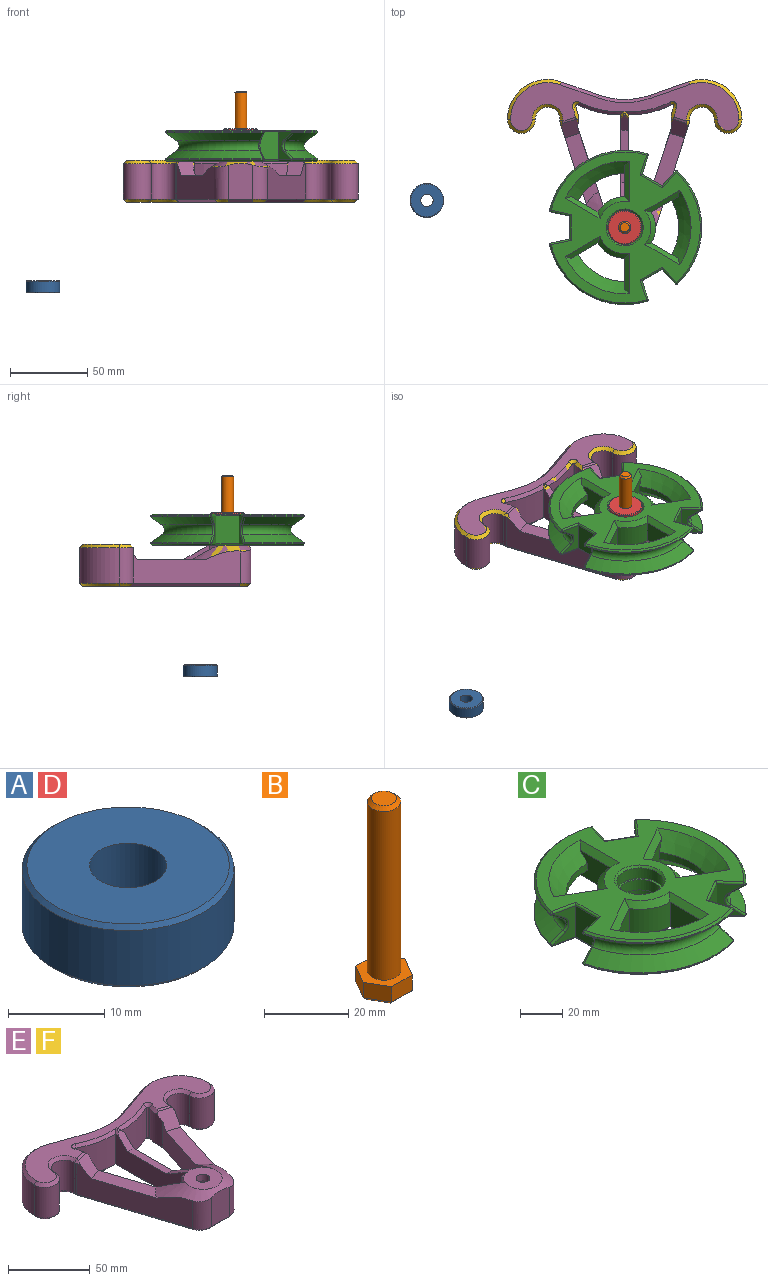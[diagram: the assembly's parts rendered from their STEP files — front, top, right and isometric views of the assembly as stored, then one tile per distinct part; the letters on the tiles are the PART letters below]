
ASSEMBLY  parts=6 mates=6
PART A: 6 faces, bbox 22x22x8 mm
  f0: cylinder r=4mm len=8mm, axis (0,0,-1), area 201.1mm2, adj f2,f3
  f1: cylinder r=11mm len=22mm, axis (0,0,-1), area 483.8mm2, adj f4,f5
  f2: plane 21x21mm, normal (0,0,1), area 296.1mm2, adj f0,f5
  f3: plane 21x21mm, normal (0,0,-1), area 296.1mm2, adj f0,f4
  f4: cone r=11mm half-angle=45deg, axis (0,0,1), area 47.8mm2, adj f1,f3
  f5: cone r=10.5mm half-angle=45deg, axis (0,0,-1), area 47.8mm2, adj f1,f2
PART B: 17 faces, bbox 13.9x12x55.5 mm
  f0: plane 6.93x4.5mm, normal (0,1,0), area 31.2mm2, adj f1,f5,f6,f15
  f1: plane 6x4.5mm, normal (-0.87,0.5,0), area 31.2mm2, adj f0,f2,f6,f16
  f2: plane 6x4.5mm, normal (-0.87,-0.5,0), area 31.2mm2, adj f1,f3,f6,f14
  f3: plane 6.93x4.5mm, normal (0,-1,0), area 31.2mm2, adj f2,f4,f6,f12
  f4: plane 6x4.5mm, normal (0.87,-0.5,0), area 31.2mm2, adj f3,f5,f6,f11
  f5: plane 6x4.5mm, normal (0.87,0.5,0), area 31.2mm2, adj f0,f4,f6,f13
  f6: plane 13.86x12mm, normal (0,0,1), area 74.4mm2, adj f0,f1,f2,f3,f4,f5,f8
  f7: plane 11.55x10mm, normal (0,0,-1), area 86.6mm2, adj f11,f12,f13,f14,f15,f16
  f8: cylinder r=4mm len=49mm, axis (0,0,-1), area 1231.5mm2, adj f6,f10
  f9: plane 6x6mm, normal (0,0,1), area 28.3mm2, adj f10
  f10: cone r=3mm half-angle=45deg, axis (0,0,-1), area 31.1mm2, adj f8,f9
  f11: plane 6x4.04mm, normal (0.61,-0.35,-0.71), area 9mm2, adj f4,f7,f12,f13
  f12: plane 6.93x1mm, normal (0,-0.71,-0.71), area 9mm2, adj f3,f7,f11,f14
  f13: plane 6x4.04mm, normal (0.61,0.35,-0.71), area 9mm2, adj f5,f7,f11,f15
  f14: plane 6x4.04mm, normal (-0.61,-0.35,-0.71), area 9mm2, adj f2,f7,f12,f16
  f15: plane 6.93x1mm, normal (0,0.71,-0.71), area 9mm2, adj f0,f7,f13,f16
  f16: plane 6x4.04mm, normal (-0.61,0.35,-0.71), area 9mm2, adj f1,f7,f14,f15
PART C: 135 faces, bbox 116.7x130.1x43.8 mm
  f0: plane 98x96.72mm, normal (0,0,-1), area 3342.2mm2, adj f33,f35,f37,f52,f54,f56,f71,f73
  f1: plane 98x96.72mm, normal (0,0,1), area 3342.2mm2, adj f28,f30,f32,f47,f49,f51,f66,f68
  f2: cone r=42.68mm half-angle=55deg, axis (0,0,-1), area 676.7mm2, adj f3,f6,f48,f50,f77,f78
  f3: cylinder r=50mm len=73.01mm, axis (0,0,1), area 48.9mm2, adj f2,f50,f77,f83
  f4: cylinder r=50mm len=73.01mm, axis (0,0,1), area 48.9mm2, adj f5,f45,f72,f92
  f5: cone r=42.68mm half-angle=55deg, axis (0,0,1), area 676.7mm2, adj f4,f6,f44,f45,f72,f74
  f6: torus R=44.97mm, axis (0,0,1), area 520.3mm2, adj f2,f5,f46,f76
  f7: cone r=42.68mm half-angle=55deg, axis (0,0,-1), area 676.7mm2, adj f8,f11,f29,f31,f58,f59
  f8: cylinder r=50mm len=63.23mm, axis (0,0,1), area 48.9mm2, adj f7,f31,f58,f86
  f9: cylinder r=50mm len=63.23mm, axis (0,0,1), area 48.9mm2, adj f10,f26,f53,f95
  f10: cone r=42.68mm half-angle=55deg, axis (0,0,1), area 676.7mm2, adj f9,f11,f25,f26,f53,f55
  f11: torus R=44.97mm, axis (0,0,1), area 520.3mm2, adj f7,f10,f27,f57
  f12: cone r=42.68mm half-angle=55deg, axis (0,0,-1), area 676.7mm2, adj f13,f16,f39,f40,f67,f69
  f13: cylinder r=50mm len=63.23mm, axis (0,0,1), area 48.9mm2, adj f12,f39,f69,f80
  f14: cylinder r=50mm len=63.23mm, axis (0,0,1), area 48.9mm2, adj f15,f34,f64,f89
  f15: cone r=42.68mm half-angle=55deg, axis (0,0,1), area 676.7mm2, adj f14,f16,f34,f36,f63,f64
  f16: torus R=44.97mm, axis (0,0,1), area 520.3mm2, adj f12,f15,f38,f65
  f17: cylinder r=11mm len=22mm, axis (0,0,1), area 414.7mm2, adj f18,f97
  f18: plane 22x22mm, normal (0,0,-1), area 66mm2, adj f17,f19
  f19: cylinder r=10mm len=20mm, axis (0,0,1), area 377mm2, adj f18,f20
  f20: plane 22x22mm, normal (0,0,1), area 66mm2, adj f19,f21
  f21: cylinder r=11mm len=22mm, axis (0,0,1), area 414.7mm2, adj f20,f98
  f22: plane 18x15mm, normal (-1,0,0), area 270mm2, adj f23,f24,f30,f35
  f23: plane 18x12.46mm, normal (-0.21,0.98,0), area 127.1mm2, adj f22,f32,f34,f36,f37,f38,f39,f40
  f24: plane 18x12.46mm, normal (-0.21,-0.98,0), area 127.1mm2, adj f22,f25,f26,f27,f28,f29,f31,f33
  f25: bspline ~34.55x25.15mm, area 13.7mm2, adj f10,f24,f26,f27
  f26: cylinder r=1mm len=1.21mm, axis (0,0,1), area 0.7mm2, adj f9,f10,f24,f25,f94
  f27: bspline ~9.28x3.43mm, area 13.3mm2, adj f11,f24,f25,f29
  f28: cylinder r=1mm len=13.46mm, axis (0.98,-0.21,0), area 20.6mm2, adj f1,f24,f30,f94
  f29: bspline ~34.55x25.15mm, area 13.7mm2, adj f7,f24,f27,f31
  f30: cylinder r=1mm len=16.62mm, axis (0,-1,0), area 24.8mm2, adj f1,f22,f28,f32
  f31: cylinder r=1mm len=1.21mm, axis (0,0,1), area 0.7mm2, adj f7,f8,f24,f29,f85
  f32: cylinder r=1mm len=13.46mm, axis (-0.98,-0.21,0), area 20.6mm2, adj f1,f23,f30,f90
  f33: cylinder r=1mm len=13.46mm, axis (-0.98,0.21,0), area 20.6mm2, adj f0,f24,f35,f85
  f34: cylinder r=1mm len=1.21mm, axis (0,0,1), area 0.7mm2, adj f14,f15,f23,f36,f90
  f35: cylinder r=1mm len=16.62mm, axis (0,1,0), area 24.8mm2, adj f0,f22,f33,f37
  f36: bspline ~34.55x25.15mm, area 13.7mm2, adj f15,f23,f34,f38
  f37: cylinder r=1mm len=13.46mm, axis (0.98,0.21,0), area 20.6mm2, adj f0,f23,f35,f81
  f38: bspline ~9.28x3.43mm, area 13.3mm2, adj f16,f23,f36,f40
  f39: cylinder r=1mm len=1.21mm, axis (0,0,1), area 0.7mm2, adj f12,f13,f23,f40,f81
  f40: bspline ~34.55x25.15mm, area 13.7mm2, adj f12,f23,f38,f39
  f41: plane 18x12.99mm, normal (0.5,0.87,0), area 270mm2, adj f42,f43,f49,f54
  f42: plane 18x12.1mm, normal (0.95,-0.31,0), area 127.1mm2, adj f41,f51,f53,f55,f56,f57,f58,f59
  f43: plane 18x9.47mm, normal (-0.74,0.67,0), area 127.1mm2, adj f41,f44,f45,f46,f47,f48,f50,f52
  f44: bspline ~26.52x25.15mm, area 13.7mm2, adj f5,f43,f45,f46
  f45: cylinder r=1mm len=1.43mm, axis (0,0,1), area 0.7mm2, adj f4,f5,f43,f44,f91
  f46: bspline ~9.28x3.09mm, area 13.3mm2, adj f6,f43,f44,f48
  f47: cylinder r=1mm len=10.74mm, axis (-0.67,-0.74,0), area 20.6mm2, adj f1,f43,f49,f91
  f48: bspline ~26.52x25.15mm, area 13.7mm2, adj f2,f43,f46,f50
  f49: cylinder r=1mm len=14.89mm, axis (-0.87,0.5,0), area 24.8mm2, adj f1,f41,f47,f51
  f50: cylinder r=1mm len=1.43mm, axis (0,0,1), area 0.7mm2, adj f2,f3,f43,f48,f82
  f51: cylinder r=1mm len=13.19mm, axis (0.31,0.95,0), area 20.6mm2, adj f1,f42,f49,f96
  f52: cylinder r=1mm len=10.74mm, axis (0.67,0.74,0), area 20.6mm2, adj f0,f43,f54,f82
  f53: cylinder r=1mm len=1.27mm, axis (0,0,1), area 0.7mm2, adj f9,f10,f42,f55,f96
  f54: cylinder r=1mm len=14.89mm, axis (0.87,-0.5,0), area 24.8mm2, adj f0,f41,f52,f56
  f55: bspline ~33.88x25.15mm, area 13.7mm2, adj f10,f42,f53,f57
  f56: cylinder r=1mm len=13.19mm, axis (-0.31,-0.95,0), area 20.6mm2, adj f0,f42,f54,f87
  f57: bspline ~9.28x3.64mm, area 13.3mm2, adj f11,f42,f55,f59
  f58: cylinder r=1mm len=1.27mm, axis (0,0,1), area 0.7mm2, adj f7,f8,f42,f59,f87
  f59: bspline ~33.88x25.15mm, area 13.7mm2, adj f7,f42,f57,f58
  f60: plane 18x12.99mm, normal (0.5,-0.87,0), area 270mm2, adj f61,f62,f68,f73
  f61: plane 18x9.47mm, normal (-0.74,-0.67,0), area 127.1mm2, adj f60,f70,f72,f74,f75,f76,f77,f78
  f62: plane 18x12.1mm, normal (0.95,0.31,0), area 127.1mm2, adj f60,f63,f64,f65,f66,f67,f69,f71
  f63: bspline ~33.88x25.15mm, area 13.7mm2, adj f15,f62,f64,f65
  f64: cylinder r=1mm len=1.27mm, axis (0,0,1), area 0.7mm2, adj f14,f15,f62,f63,f88
  f65: bspline ~9.28x3.64mm, area 13.3mm2, adj f16,f62,f63,f67
  f66: cylinder r=1mm len=13.19mm, axis (-0.31,0.95,0), area 20.6mm2, adj f1,f62,f68,f88
  f67: bspline ~33.88x25.15mm, area 13.7mm2, adj f12,f62,f65,f69
  f68: cylinder r=1mm len=14.89mm, axis (0.87,0.5,0), area 24.8mm2, adj f1,f60,f66,f70
  f69: cylinder r=1mm len=1.27mm, axis (0,0,1), area 0.7mm2, adj f12,f13,f62,f67,f79
  f70: cylinder r=1mm len=10.74mm, axis (0.67,-0.74,0), area 20.6mm2, adj f1,f61,f68,f93
  f71: cylinder r=1mm len=13.19mm, axis (0.31,-0.95,0), area 20.6mm2, adj f0,f62,f73,f79
  f72: cylinder r=1mm len=1.43mm, axis (0,0,1), area 0.7mm2, adj f4,f5,f61,f74,f93
  f73: cylinder r=1mm len=14.89mm, axis (-0.87,-0.5,0), area 24.8mm2, adj f0,f60,f71,f75
  f74: bspline ~26.52x25.15mm, area 13.7mm2, adj f5,f61,f72,f76
  f75: cylinder r=1mm len=10.74mm, axis (-0.67,0.74,0), area 20.6mm2, adj f0,f61,f73,f84
  f76: bspline ~9.28x3.09mm, area 13.3mm2, adj f6,f61,f74,f78
  f77: cylinder r=1mm len=1.43mm, axis (0,0,1), area 0.7mm2, adj f2,f3,f61,f78,f84
  f78: bspline ~26.52x25.15mm, area 13.7mm2, adj f2,f61,f76,f77
  f79: bspline ~1.27x1.07mm, area 0.8mm2, adj f69,f71,f80
  f80: cone r=50mm half-angle=45deg, axis (0,0,1), area 114.6mm2, adj f0,f13,f79,f81
  f81: bspline ~1.21x1.02mm, area 0.8mm2, adj f37,f39,f80
  f82: bspline ~1.43x1.02mm, area 0.8mm2, adj f50,f52,f83
  f83: cone r=50mm half-angle=45deg, axis (0,0,1), area 114.6mm2, adj f0,f3,f82,f84
  f84: bspline ~1.43x1.02mm, area 0.8mm2, adj f75,f77,f83
  f85: bspline ~1.21x1.02mm, area 0.8mm2, adj f31,f33,f86
  f86: cone r=50mm half-angle=45deg, axis (0,0,1), area 114.6mm2, adj f0,f8,f85,f87
  f87: bspline ~1.27x1.07mm, area 0.8mm2, adj f56,f58,f86
  f88: bspline ~1.27x1.07mm, area 0.8mm2, adj f64,f66,f89
  f89: cone r=49mm half-angle=45deg, axis (0,0,-1), area 114.6mm2, adj f1,f14,f88,f90
  f90: bspline ~1.21x1.02mm, area 0.8mm2, adj f32,f34,f89
  f91: bspline ~1.43x1.02mm, area 0.8mm2, adj f45,f47,f92
  f92: cone r=49mm half-angle=45deg, axis (0,0,-1), area 114.6mm2, adj f1,f4,f91,f93
  f93: bspline ~1.43x1.02mm, area 0.8mm2, adj f70,f72,f92
  f94: bspline ~1.21x1.02mm, area 0.8mm2, adj f26,f28,f95
  f95: cone r=49mm half-angle=45deg, axis (0,0,-1), area 114.6mm2, adj f1,f9,f94,f96
  f96: bspline ~1.27x1.07mm, area 0.8mm2, adj f51,f53,f95
  f97: cone r=12mm half-angle=45deg, axis (0,0,-1), area 102.2mm2, adj f0,f17
  f98: cone r=11mm half-angle=45deg, axis (0,0,1), area 102.2mm2, adj f1,f21
  f99: plane 20x14mm, normal (-1,0,0), area 235mm2, adj f100,f102,f103,f108,f109,f110
  f100: cylinder r=35mm len=30.31mm, axis (0,0,1), area 146.6mm2, adj f99,f101,f109,f110
  f101: plane 17.32x14mm, normal (0.5,0.87,0), area 235mm2, adj f100,f102,f105,f106,f109,f110
  f102: cylinder r=20mm len=17.32mm, axis (0,0,1), area 293.2mm2, adj f99,f101,f104,f107
  f103: plane 26.4x3.24mm, normal (-0.71,0,-0.71), area 97.8mm2, adj f0,f99,f104,f109
  f104: cone r=20mm half-angle=45deg, axis (0,0,1), area 95.7mm2, adj f0,f102,f103,f105
  f105: plane 22.89x14.47mm, normal (0.35,0.61,-0.71), area 97.8mm2, adj f0,f101,f104,f109
  f106: plane 22.89x14.47mm, normal (0.35,0.61,0.71), area 97.8mm2, adj f1,f101,f107,f110
  f107: cone r=20mm half-angle=45deg, axis (0,0,-1), area 95.7mm2, adj f1,f102,f106,f108
  f108: plane 26.4x3.24mm, normal (-0.71,0,0.71), area 97.8mm2, adj f1,f99,f107,f110
  f109: cone r=43mm half-angle=45deg, axis (0,0,-1), area 474.5mm2, adj f0,f99,f100,f101,f103,f105
  f110: cone r=43mm half-angle=45deg, axis (0,0,1), area 474.5mm2, adj f1,f99,f100,f101,f106,f108
  f111: plane 17.32x14mm, normal (0.5,0.87,0), area 235mm2, adj f112,f114,f115,f120,f121,f122
  f112: cylinder r=35mm len=35mm, axis (0,0,1), area 146.6mm2, adj f111,f113,f121,f122
  f113: plane 17.32x14mm, normal (0.5,-0.87,0), area 235mm2, adj f112,f114,f117,f118,f121,f122
  f114: cylinder r=20mm len=20mm, axis (0,0,1), area 293.2mm2, adj f111,f113,f116,f119
  f115: plane 22.89x14.28mm, normal (0.35,0.61,-0.71), area 97.8mm2, adj f0,f111,f116,f121
  f116: cone r=20mm half-angle=45deg, axis (0,0,1), area 95.7mm2, adj f0,f114,f115,f117
  f117: plane 22.89x14.28mm, normal (0.35,-0.61,-0.71), area 97.8mm2, adj f0,f113,f116,f121
  f118: plane 22.89x14.28mm, normal (0.35,-0.61,0.71), area 97.8mm2, adj f1,f113,f119,f122
  f119: cone r=20mm half-angle=45deg, axis (0,0,-1), area 95.7mm2, adj f1,f114,f118,f120
  f120: plane 22.89x14.28mm, normal (0.35,0.61,0.71), area 97.8mm2, adj f1,f111,f119,f122
  f121: cone r=43mm half-angle=45deg, axis (0,0,-1), area 474.5mm2, adj f0,f111,f112,f113,f115,f117
  f122: cone r=43mm half-angle=45deg, axis (0,0,1), area 474.5mm2, adj f1,f111,f112,f113,f118,f120
  f123: plane 17.32x14mm, normal (0.5,-0.87,0), area 235mm2, adj f124,f126,f127,f132,f133,f134
  f124: cylinder r=35mm len=30.31mm, axis (0,0,1), area 146.6mm2, adj f123,f125,f133,f134
  f125: plane 20x14mm, normal (-1,0,0), area 235mm2, adj f124,f126,f129,f130,f133,f134
  f126: cylinder r=20mm len=17.32mm, axis (0,0,1), area 293.2mm2, adj f123,f125,f128,f131
  f127: plane 22.89x14.47mm, normal (0.35,-0.61,-0.71), area 97.8mm2, adj f0,f123,f128,f133
  f128: cone r=20mm half-angle=45deg, axis (0,0,1), area 95.7mm2, adj f0,f126,f127,f129
  f129: plane 26.4x3.24mm, normal (-0.71,0,-0.71), area 97.8mm2, adj f0,f125,f128,f133
  f130: plane 26.4x3.24mm, normal (-0.71,0,0.71), area 97.8mm2, adj f1,f125,f131,f134
  f131: cone r=20mm half-angle=45deg, axis (0,0,-1), area 95.7mm2, adj f1,f126,f130,f132
  f132: plane 22.89x14.47mm, normal (0.35,-0.61,0.71), area 97.8mm2, adj f1,f123,f131,f134
  f133: cone r=43mm half-angle=45deg, axis (0,0,-1), area 474.5mm2, adj f0,f123,f124,f125,f127,f129
  f134: cone r=43mm half-angle=45deg, axis (0,0,1), area 474.5mm2, adj f1,f123,f124,f125,f130,f132
PART D: same geometry as A
PART E: 97 faces, bbox 152.4x125.5x27.5 mm
  f0: plane 148x31mm, normal (0,0,1), area 1955.9mm2, adj f75,f76,f77,f78,f79,f80,f81,f82
  f1: plane 75.66x24.54mm, normal (0.95,-0.31,0), area 1337.3mm2, adj f14,f15,f54,f56,f58,f74,f93
  f2: cylinder r=20mm len=22.5mm, axis (0,0,-1), area 288.5mm2, adj f3,f40,f50,f58,f96
  f3: plane 60.67x24.45mm, normal (-0.95,0.31,0), area 1038.3mm2, adj f2,f36,f48,f54,f56,f58
  f4: plane 75.66x24.54mm, normal (-0.95,-0.31,0), area 1337.3mm2, adj f11,f12,f54,f55,f57,f67,f76
  f5: plane 23.5x23.5mm, normal (0,0,1), area 377mm2, adj f7,f52,f54
  f6: plane 148x107mm, normal (0,0,-1), area 3207.1mm2, adj f22,f23,f24,f25,f26,f27,f34,f35
  f7: cylinder r=4.25mm len=8.5mm, axis (0,0,-1), area 133.5mm2, adj f5,f28
  f8: cylinder r=26mm len=34.61mm, axis (0,0,-1), area 1141.3mm2, adj f9,f21,f59,f79
  f9: cylinder r=9mm len=23mm, axis (0,0,-1), area 650.3mm2, adj f8,f10,f61,f77
  f10: cylinder r=8mm len=23mm, axis (0,0,-1), area 590.5mm2, adj f9,f11,f63,f75
  f11: cylinder r=5mm len=23mm, axis (0,0,-1), area 43.9mm2, adj f4,f10,f65,f76
  f12: cylinder r=10mm len=22.04mm, axis (0,0,-1), area 264.8mm2, adj f4,f13,f54,f69
  f13: plane 23.13x15.48mm, normal (0,-1,0), area 351.8mm2, adj f12,f14,f54,f71
  f14: cylinder r=10mm len=22.04mm, axis (0,0,-1), area 264.8mm2, adj f1,f13,f54,f73
  f15: cylinder r=5mm len=23mm, axis (0,0,-1), area 43.9mm2, adj f1,f16,f72,f93
  f16: cylinder r=8mm len=23mm, axis (0,0,-1), area 590.5mm2, adj f15,f17,f70,f91
  f17: cylinder r=9mm len=23mm, axis (0,0,-1), area 650.3mm2, adj f16,f18,f68,f89
  f18: cylinder r=26mm len=34.61mm, axis (0,0,-1), area 1141.3mm2, adj f17,f19,f66,f87
  f19: plane 24.82x23mm, normal (-0.33,0.94,0), area 605.1mm2, adj f18,f20,f64,f85
  f20: cylinder r=50mm len=33.13mm, axis (0,0,-1), area 776.7mm2, adj f19,f21,f62,f83
  f21: plane 24.82x23mm, normal (0.33,0.94,0), area 605.1mm2, adj f8,f20,f60,f81
  f22: plane 22x6.75mm, normal (-0.87,-0.5,0), area 171.5mm2, adj f6,f23,f27,f28
  f23: plane 22x6.75mm, normal (-0.87,0.5,0), area 171.5mm2, adj f6,f22,f24,f28
  f24: plane 22x7.79mm, normal (0,1,0), area 171.5mm2, adj f6,f23,f25,f28
  f25: plane 22x6.75mm, normal (0.87,0.5,0), area 171.5mm2, adj f6,f24,f26,f28
  f26: plane 22x6.75mm, normal (0.87,-0.5,0), area 171.5mm2, adj f6,f25,f27,f28
  f27: plane 22x7.79mm, normal (0,-1,0), area 171.5mm2, adj f6,f22,f26,f28
  f28: plane 15.59x13.5mm, normal (0,0,-1), area 101.1mm2, adj f7,f22,f23,f24,f25,f26,f27
  f29: plane 60.67x24.45mm, normal (0.95,0.31,0), area 1038.3mm2, adj f30,f35,f41,f54,f55,f57
  f30: cylinder r=20mm len=22.5mm, axis (0,0,-1), area 288.5mm2, adj f29,f31,f42,f57,f80
  f31: cylinder r=1mm len=22.5mm, axis (0,0,-1), area 55.4mm2, adj f30,f32,f43,f82
  f32: cylinder r=60mm len=27.89mm, axis (0,0,-1), area 650.7mm2, adj f31,f33,f44,f84
  f33: plane 61.26x24.37mm, normal (-1,0,0), area 1021.4mm2, adj f32,f34,f45,f51,f52,f53,f86
  f34: plane 27.29x7.23mm, normal (0,1,0), area 116.5mm2, adj f6,f33,f35,f45,f52
  f35: plane 27.05x10.04mm, normal (-0.87,0.5,0), area 222.3mm2, adj f6,f29,f34,f41,f52,f54
  f36: plane 27.05x10.04mm, normal (0.87,0.5,0), area 222.3mm2, adj f3,f6,f37,f48,f52,f54
  f37: plane 27.3x7.24mm, normal (0,1,0), area 116.5mm2, adj f6,f36,f38,f46,f52
  f38: plane 61.26x24.37mm, normal (1,0,0), area 1021.4mm2, adj f37,f39,f46,f51,f52,f53,f90
  f39: cylinder r=60mm len=27.89mm, axis (0,0,-1), area 650.7mm2, adj f38,f40,f47,f92
  f40: cylinder r=1mm len=22.5mm, axis (0,0,-1), area 55.4mm2, adj f2,f39,f49,f94
  f41: plane 63.62x22.32mm, normal (0.67,0.22,-0.71), area 230.8mm2, adj f6,f29,f35,f42
  f42: cone r=20mm half-angle=45deg, axis (0,0,1), area 44.8mm2, adj f6,f30,f41,f43
  f43: cone r=3.5mm half-angle=45deg, axis (0,0,-1), area 19.6mm2, adj f6,f31,f42,f44
  f44: cone r=60mm half-angle=45deg, axis (0,0,1), area 104.6mm2, adj f6,f32,f43,f45
  f45: plane 63.88x2.55mm, normal (-0.71,0,-0.71), area 221.1mm2, adj f33,f34,f44,f46
  f46: plane 63.88x2.55mm, normal (0.71,0,-0.71), area 221.1mm2, adj f37,f38,f45,f47
  f47: cone r=57.5mm half-angle=45deg, axis (0,0,1), area 104.6mm2, adj f6,f39,f46,f49
  f48: plane 63.62x22.32mm, normal (-0.67,0.22,-0.71), area 230.8mm2, adj f3,f6,f36,f50
  f49: cone r=1mm half-angle=45deg, axis (0,0,-1), area 19.6mm2, adj f6,f40,f47,f50
  f50: cone r=17.5mm half-angle=45deg, axis (0,0,1), area 44.8mm2, adj f2,f6,f48,f49
  f51: plane 34.03x5mm, normal (0,0,1), area 169.7mm2, adj f33,f38,f52,f53
  f52: cone r=29.07mm half-angle=60deg, axis (0,0,-1), area 118.2mm2, adj f5,f33,f34,f35,f36,f37,f38,f51
  f53: cone r=72.99mm half-angle=45deg, axis (0,0,1), area 63.9mm2, adj f33,f38,f51,f86,f88,f90
  f54: cone r=29.07mm half-angle=60deg, axis (0,0,-1), area 797.2mm2, adj f1,f3,f4,f5,f12,f13,f14,f29
  f55: plane 45.97x21.7mm, normal (0,0,1), area 418.5mm2, adj f4,f29,f54,f57
  f56: plane 45.97x21.7mm, normal (0,0,1), area 418.5mm2, adj f1,f3,f54,f58
  f57: plane 12.54x12.05mm, normal (0.22,-0.67,0.71), area 138.3mm2, adj f4,f29,f30,f55,f76,f78,f80
  f58: plane 12.54x12.05mm, normal (-0.22,-0.67,0.71), area 138.3mm2, adj f1,f2,f3,f56,f93,f95,f96
  f59: cone r=24mm half-angle=45deg, axis (0,0,1), area 134.9mm2, adj f6,f8,f60,f61
  f60: plane 25.48x10.6mm, normal (0.23,0.67,-0.71), area 74.4mm2, adj f6,f21,f59,f62
  f61: cone r=9mm half-angle=45deg, axis (0,0,1), area 71.1mm2, adj f6,f9,f59,f63
  f62: cone r=52mm half-angle=45deg, axis (0,0,-1), area 97.4mm2, adj f6,f20,f60,f64
  f63: cone r=8mm half-angle=45deg, axis (0,0,-1), area 81.7mm2, adj f6,f10,f61,f65
  f64: plane 25.48x10.6mm, normal (-0.23,0.67,-0.71), area 74.4mm2, adj f6,f19,f62,f66
  f65: cone r=5mm half-angle=45deg, axis (0,0,1), area 4.3mm2, adj f6,f11,f63,f67
  f66: cone r=26mm half-angle=45deg, axis (0,0,1), area 134.9mm2, adj f6,f18,f64,f68
  f67: plane 76.28x26.45mm, normal (-0.67,-0.22,-0.71), area 225mm2, adj f4,f6,f65,f69
  f68: cone r=7mm half-angle=45deg, axis (0,0,1), area 71.1mm2, adj f6,f17,f66,f70
  f69: cone r=10mm half-angle=45deg, axis (0,0,1), area 32mm2, adj f6,f12,f67,f71
  f70: cone r=10mm half-angle=45deg, axis (0,0,-1), area 81.7mm2, adj f6,f16,f68,f72
  f71: plane 15.46x2mm, normal (0,-0.71,-0.71), area 43.7mm2, adj f6,f13,f69,f73
  f72: cone r=5mm half-angle=45deg, axis (0,0,1), area 4.3mm2, adj f6,f15,f70,f74
  f73: cone r=10mm half-angle=45deg, axis (0,0,1), area 32mm2, adj f6,f14,f71,f74
  f74: plane 76.28x26.45mm, normal (0.67,-0.22,-0.71), area 225mm2, adj f1,f6,f72,f73
  f75: cone r=10mm half-angle=45deg, axis (0,0,1), area 81.7mm2, adj f0,f10,f76,f77
  f76: cone r=3mm half-angle=45deg, axis (0,0,-1), area 7.1mm2, adj f0,f4,f11,f57,f75,f78
  f77: cone r=7mm half-angle=45deg, axis (0,0,-1), area 71.1mm2, adj f0,f9,f75,f79
  f78: plane 8.88x4.21mm, normal (0.12,-0.36,0.92), area 13.6mm2, adj f0,f57,f76,f80
  f79: cone r=26mm half-angle=45deg, axis (0,0,-1), area 134.9mm2, adj f0,f8,f77,f81
  f80: cone r=20mm half-angle=45deg, axis (0,0,-1), area 22.2mm2, adj f0,f30,f57,f78,f82
  f81: plane 25.48x10.6mm, normal (0.23,0.67,0.71), area 74.4mm2, adj f0,f21,f79,f83
  f82: cone r=3mm half-angle=45deg, axis (0,0,1), area 13.9mm2, adj f0,f31,f80,f84
  f83: cone r=50mm half-angle=45deg, axis (0,0,1), area 97.4mm2, adj f0,f20,f81,f85
  f84: cone r=60mm half-angle=45deg, axis (0,0,-1), area 83.3mm2, adj f0,f32,f82,f86
  f85: plane 25.48x10.6mm, normal (-0.23,0.67,0.71), area 74.4mm2, adj f0,f19,f83,f87
  f86: plane 4.13x2.03mm, normal (-0.71,0,0.71), area 5.4mm2, adj f0,f33,f53,f84,f88
  f87: cone r=24mm half-angle=45deg, axis (0,0,-1), area 134.9mm2, adj f0,f18,f85,f89
  f88: cone r=72.41mm half-angle=67.5deg, axis (0,0,1), area 2.4mm2, adj f0,f53,f86,f90
  f89: cone r=9mm half-angle=45deg, axis (0,0,-1), area 71.1mm2, adj f0,f17,f87,f91
  f90: plane 4.13x2.03mm, normal (0.71,0,0.71), area 5.4mm2, adj f0,f38,f53,f88,f92
  f91: cone r=8mm half-angle=45deg, axis (0,0,1), area 81.7mm2, adj f0,f16,f89,f93
  f92: cone r=58mm half-angle=45deg, axis (0,0,-1), area 83.3mm2, adj f0,f39,f90,f94
  f93: cone r=3mm half-angle=45deg, axis (0,0,-1), area 7.1mm2, adj f0,f1,f15,f58,f91,f95
  f94: cone r=1mm half-angle=45deg, axis (0,0,1), area 13.9mm2, adj f0,f40,f92,f96
  f95: plane 8.88x4.21mm, normal (-0.12,-0.36,0.92), area 13.6mm2, adj f0,f58,f93,f96
  f96: cone r=18mm half-angle=45deg, axis (0,0,-1), area 22.2mm2, adj f0,f2,f58,f94,f95
PART F: same geometry as E
PLACE A t=(32.57,-36.32,-42.71)mm
PLACE B t=(160.75,-54,32.62)mm
PLACE C rot(axis=(0,0,-1),0deg) t=(160.75,-54,52.62)mm
PLACE D rot(axis=(0,0,-1),0deg) t=(160.75,-54,55.62)mm
PLACE E t=(160.75,-54,16.12)mm fixed
PLACE F t=(160.75,-54,16.12)mm
MATE slider D.f1 <-> C.f2  axis (0,0,-1) through (160.75,-54,59.62)mm
MATE planar A.f1 <-> C.f2  axis (0,0,1) through (32.57,-36.32,-34.71)mm
MATE revolute A.f1 <-> C.f2  axis (0,0,-1) through (32.57,-36.32,-38.71)mm
MATE cylindrical C.f112 <-> B.f8  axis (0,0,1) through (160.75,-54,62.62)mm
MATE cylindrical B.f8 <-> E.f7  axis (0,0,-1) through (160.75,-54,38.12)mm
MATE planar D.f1 <-> C.f100  axis (0,0,-1) through (160.75,-54,55.62)mm
